# Revit family: CSBRADA-6030-3F
name_source: partatom
category: Plumbing Fixtures
revit_build: Autodesk Revit MEP 2016 (Build: 20150220_1215(x64)
units: mm (PartAtom-declared; Revit-internal decimal feet)

## family parameters
Cut with Voids When Loaded = No
Host = Face
OmniClass Number = 23.45.05.14.17.14
OmniClass Title = Shower Receptors
Part Type = Normal
Room Calculation Point = No
Round Connector Dimension = Use Diameter
Shared = Yes

## types (1)
- CSBRADA-6030-3F
    Amperage = 0
    CSBRADA-6030-3F - 60 X 30" ADA Corterrra Shower Base Rectangular Roll-in Type = Yes
    CW Connection = No
    Default Elevation = -2"
    Description = 60 X 30" ADA Corterrra Shower Base Rectangular Roll-in Type
    HW Connection = No
    Manufacturer = Acorn Engineering Co.
    Material = Corterra
    Model = CSBRADA-6030-3F
    Revised Date = 03/16/17
    Tempered Water Connection = No
    URL = https://www.acorneng.com
    Vent Connection = No
    Voltage = 0
    Waste Connection = Yes

## geometry (parser evidence)
native form markers: Sweep x7
no freeform markers — native parametric forms only
